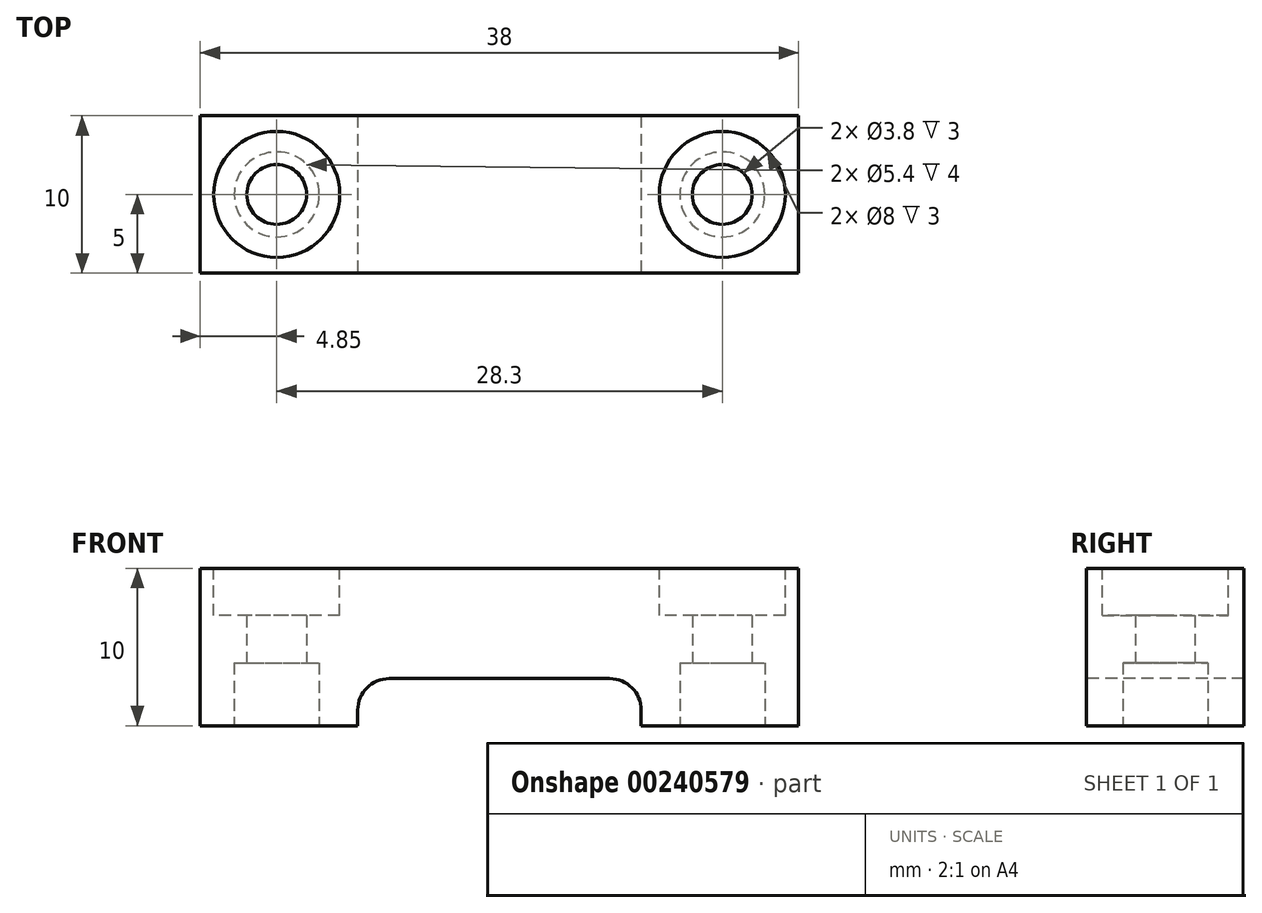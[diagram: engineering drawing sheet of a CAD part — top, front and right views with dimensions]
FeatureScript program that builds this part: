
annotation { "Feature Type Name" : "Feature", "Feature Type Description" : "" }
export const myFeature = defineFeature(function(context is Context, id is Id, definition is map)
    precondition{}
    {
        {
            var Q0;
            Q0=qCreatedBy(makeId("Top.planeOp"),FACE);
            var sketch = newSketch(context, id + "F0", { "sketchPlane" : qUnion([Q0])});
            skLineSegment(sketch, "E0.bottom", {"start": v(-19, 5) * mm, "end": v(19, 5) * mm});
            skLineSegment(sketch, "E0.top", {"start": v(-19, -5) * mm, "end": v(19, -5) * mm});
            skLineSegment(sketch, "E0.left", {"start": v(-19, 5) * mm, "end": v(-19, -5) * mm});
            skLineSegment(sketch, "E0.right", {"start": v(19, 5) * mm, "end": v(19, -5) * mm});
            skCircle(sketch, "E1", {"center": v(-14.15, 0) * mm, "radius": 1.9 * mm});
            skCircle(sketch, "E2", {"center": v(14.15, 0) * mm, "radius": 1.9 * mm});
            skSolve(sketch);
        }
        {
            var Q0;
            Q0 = qSketchRegion(id + "F0", true);
            extrude(context, id + "F1", {"entities" : qUnion([Q0]), "depth" : 10 * mm});
        }
        {
            var Q0;
            Q0=makeQuery(id+"F1.opExtrude","SWEPT_FACE",FACE,{"disambiguationData":[OSD([sQuery(id+"F0.wireOp",EDGE,"E0.top")])]});
            var sketch = newSketch(context, id + "F2", { "sketchPlane" : qUnion([Q0])});
            skLineSegment(sketch, "E3.bottom", {"start": v(-9, 0) * mm, "end": v(9, 0) * mm});
            skLineSegment(sketch, "E3.top", {"start": v(-9, 3) * mm, "end": v(9, 3) * mm});
            skLineSegment(sketch, "E3.left", {"start": v(-9, 0) * mm, "end": v(-9, 3) * mm});
            skLineSegment(sketch, "E3.right", {"start": v(9, 0) * mm, "end": v(9, 3) * mm});
            skSolve(sketch);
        }
        {
            var Q0;
            Q0 = qSketchRegion(id + "F2", true);
            extrude(context, id + "F3", {"entities" : qUnion([Q0]), "operationType" : NewBodyOperationType.REMOVE, "endBound" : BoundingType.THROUGH_ALL, "oppositeDirection" : true, "depth" : 25 * mm});
        }
        {
            var Q0;
            {var subQ0=sQuery(id+"F0.wireOp",EDGE,"E1");var subQ1=sQuery(id+"F0.wireOp",EDGE,"E0.left");var subQ2=sQuery(id+"F0.wireOp",EDGE,"E0.top");var subQ3=sQuery(id+"F0.wireOp",EDGE,"E0.bottom");Q0=makeQuery(id+"F3.boolean.opBoolean","SPLIT",FACE,{"disambiguationData":[TD([makeQuery(id+"F1.opExtrude","SWEPT_FACE",FACE,{"disambiguationData":[OSD([subQ1])]})])],"derivedFrom":makeQuery(id+"F1.opExtrude","CAP_FACE",FACE,{"disambiguationData":[OSD([subQ3,subQ2,subQ1,sQuery(id+"F0.wireOp",EDGE,"E0.right"),subQ0,sQuery(id+"F0.wireOp",EDGE,"E2")])],"isStart":true})});}
            var sketch = newSketch(context, id + "F4", { "sketchPlane" : qUnion([Q0])});
            skCircle(sketch, "E4", {"center": v(-14.15, 0) * mm, "radius": 2.7 * mm});
            skCircle(sketch, "E5", {"center": v(14.15, 0) * mm, "radius": 2.7 * mm});
            skSolve(sketch);
        }
        {
            var Q0;
            Q0 = qSketchRegion(id + "F4", true);
            extrude(context, id + "F5", {"entities" : qUnion([Q0]), "operationType" : NewBodyOperationType.REMOVE, "oppositeDirection" : true, "depth" : 4 * mm});
        }
        {
            var Q0;
            Q0=makeQuery(id+"F3.boolean.opBoolean","COPY",EDGE,{"derivedFrom":makeQuery(id+"F3.opExtrude","SWEPT_EDGE",EDGE,{"disambiguationData":[OSD([sQuery(id+"F2.wireOp",EDGE,"E3.top"),sQuery(id+"F2.wireOp",EDGE,"E3.left")])]})});
            var Q1;
            Q1=makeQuery(id+"F3.boolean.opBoolean","COPY",EDGE,{"derivedFrom":makeQuery(id+"F3.opExtrude","SWEPT_EDGE",EDGE,{"disambiguationData":[OSD([sQuery(id+"F2.wireOp",EDGE,"E3.top"),sQuery(id+"F2.wireOp",EDGE,"E3.right")])]})});
            fillet(context, id + "F6", {"entities" : qUnion([Q0, Q1]), "radius" : 2 * mm, "tangentPropagation" : true, "allowEdgeOverflow" : false});
        }
        {
            var Q0;
            Q0=makeQuery(id+"F1.opExtrude","CAP_FACE",FACE,{"disambiguationData":[OSD([sQuery(id+"F0.wireOp",EDGE,"E0.bottom"),sQuery(id+"F0.wireOp",EDGE,"E0.top"),sQuery(id+"F0.wireOp",EDGE,"E0.left"),sQuery(id+"F0.wireOp",EDGE,"E0.right"),sQuery(id+"F0.wireOp",EDGE,"E1"),sQuery(id+"F0.wireOp",EDGE,"E2")])],"isStart":false});
            var sketch = newSketch(context, id + "F7", { "sketchPlane" : qUnion([Q0])});
            skCircle(sketch, "E6", {"center": v(-14.15, 0) * mm, "radius": 4 * mm});
            skCircle(sketch, "E7", {"center": v(14.15, 0) * mm, "radius": 4 * mm});
            skSolve(sketch);
        }
        {
            var Q0;
            Q0 = qSketchRegion(id + "F7", true);
            extrude(context, id + "F8", {"entities" : qUnion([Q0]), "operationType" : NewBodyOperationType.REMOVE, "oppositeDirection" : true, "depth" : 3 * mm});
        }
    });
